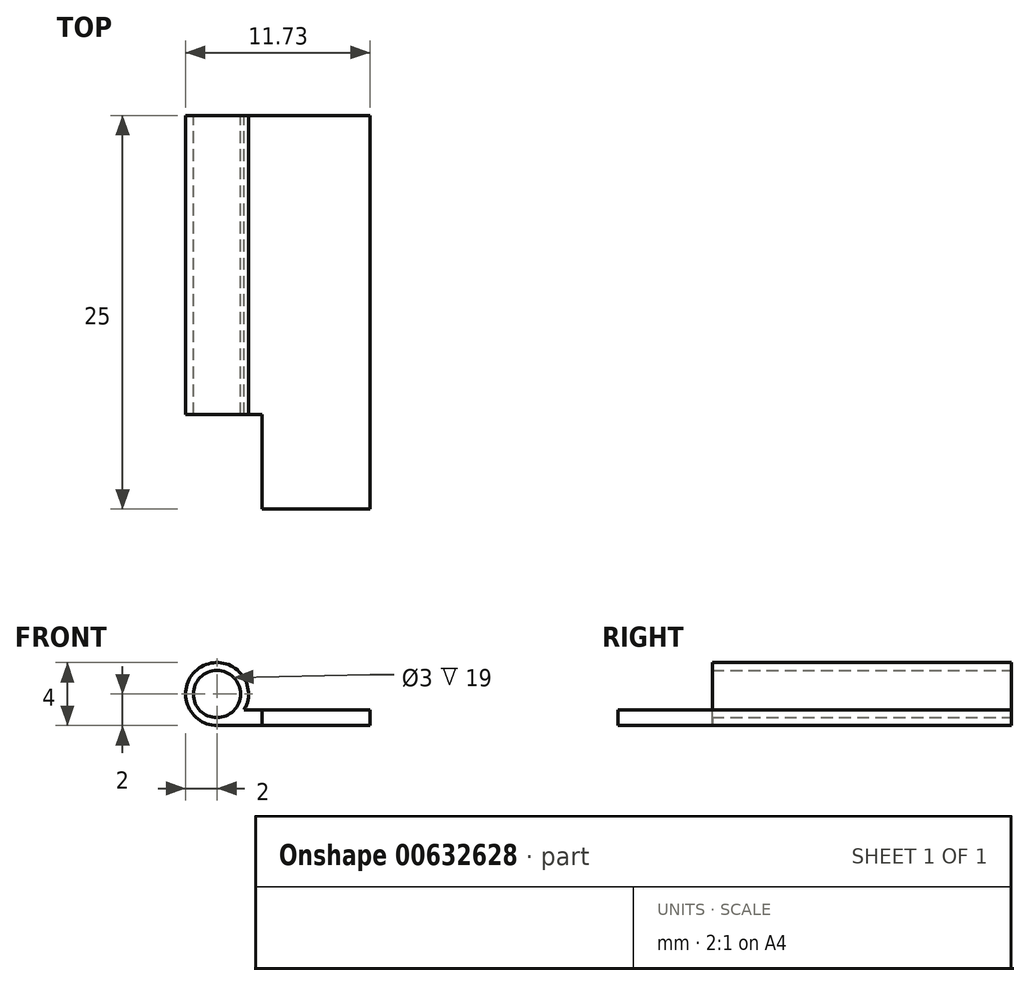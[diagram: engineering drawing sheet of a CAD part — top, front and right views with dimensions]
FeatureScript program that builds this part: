
annotation { "Feature Type Name" : "Feature", "Feature Type Description" : "" }
export const myFeature = defineFeature(function(context is Context, id is Id, definition is map)
    precondition{}
    {
        {
            var Q0;
            Q0=qCreatedBy(makeId("Front.planeOp"),FACE);
            var sketch = newSketch(context, id + "F0", { "sketchPlane" : qUnion([Q0])});
            skPoint(sketch, "E0.orphan", {"position": v(0, -1.5) * mm});
            skLineSegment(sketch, "E1", {"start": v(0, -2) * mm, "end": v(9.73, -2) * mm});
            skLineSegment(sketch, "E2.0", {"start": v(1.73, -1) * mm, "end": v(9.73, -1) * mm});
            skLineSegment(sketch, "E3", {"start": v(9.73, -1) * mm, "end": v(9.73, -2) * mm});
            skArc(sketch, "E4", {"start": v(1.73, -1) * mm, "mid": v(-1, 1.73) * mm, "end": v(0, -2) * mm});
            skCircle(sketch, "E5", {"center": v(0, 0) * mm, "radius": 1.5 * mm});
            skSolve(sketch);
        }
        {
            var Q0;
            Q0 = qSketchRegion(id + "F0", true);
            extrude(context, id + "F1", {"entities" : qUnion([Q0]), "depth" : 25 * mm, "offsetDistance" : 25 * mm, "symmetric" : true});
        }
        {
            var Q0;
            Q0=makeQuery(id+"F1.opExtrude","CAP_FACE",FACE,{"disambiguationData":[OSD([sQuery(id+"F0.wireOp",EDGE,"E1"),sQuery(id+"F0.wireOp",EDGE,"E2.0"),sQuery(id+"F0.wireOp",EDGE,"E3"),sQuery(id+"F0.wireOp",EDGE,"E4"),sQuery(id+"F0.wireOp",EDGE,"E5")])],"isStart":false});
            var sketch = newSketch(context, id + "F2", { "sketchPlane" : qUnion([Q0])});
            skLineSegment(sketch, "E6.top", {"start": v(1.73, 2.81) * mm, "end": v(2.85, 2.81) * mm});
            skLineSegment(sketch, "E6.right", {"start": v(2.85, -1) * mm, "end": v(2.85, 2.81) * mm});
            skLineSegment(sketch, "E7.right", {"start": v(2.85, -2.6) * mm, "end": v(2.85, -1) * mm});
            skLineSegment(sketch, "E8.bottom", {"start": v(1.73, 2.81) * mm, "end": v(-4.35, 2.81) * mm});
            skLineSegment(sketch, "E8.top", {"start": v(1.73, -3.38) * mm, "end": v(-4.35, -3.38) * mm});
            skLineSegment(sketch, "E8.right", {"start": v(-4.35, 2.81) * mm, "end": v(-4.35, -3.38) * mm});
            skPoint(sketch, "E8.left.end.orphan", {"position": v(1.73, -2.6) * mm});
            skLineSegment(sketch, "E9", {"start": v(2.85, -2.6) * mm, "end": v(1.73, -3.38) * mm});
            skSolve(sketch);
        }
        {
            var Q0;
            Q0 = qSketchRegion(id + "F2", true);
            extrude(context, id + "F3", {"entities" : qUnion([Q0]), "operationType" : NewBodyOperationType.REMOVE, "oppositeDirection" : true, "depth" : 6 * mm, "offsetDistance" : 25 * mm});
        }
    });
